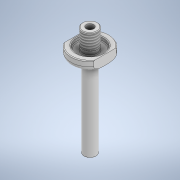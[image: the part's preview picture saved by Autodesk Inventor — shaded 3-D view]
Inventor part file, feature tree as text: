
AUTODESK INVENTOR PART (.ipt)
format: ipt  version: 2021 (Build 250183000, 183)  size: 212,992 bytes
history: native  units: mm
features: extrude x6, sketch x6, fillet x5, chamfer x2, thread x1, projected_geometry x1
ambient origin geometry x8: Origin, YZ Plane, XZ Plane, XY Plane, X Axis, Y Axis, Z Axis, Center Point
bodies: Solid1 (feature_tree)
feature tree (21):
  extrude  "Extrusion1"  Depth=3.2mm TaperAngle=0.0deg
  extrude  "Extrusion2"  Depth=0.25mm
  fillet  "Fillet1"  Radius=1.32mm
  fillet  "Fillet6"  Radius=0.25mm
  extrude  "Extrusion3"  Depth=2.0mm TaperAngle=0.0deg
  chamfer  "Chamfer2"  Distance=2.0mm Angle=45.0deg
  chamfer  "Chamfer3"  Distance=2.0mm Angle=45.0deg
  extrude  "Extrusion4"  Depth=27.5mm TaperAngle=0.0deg
  extrude  "Extrusion5"  TaperAngle=0.0deg  [1 undecoded]
  thread  "Thread1"  [1 undecoded]
  fillet  "Fillet2"  Radius=0.219mm
  fillet  "Fillet3"  Radius=0.248mm
  extrude  "Extrusion6"  Depth=10.0mm TaperAngle=0.0deg
  fillet  "Fillet5"  Radius=0.25mm
  sketch  "Sketch1"  dims[d0=12.5mm d1=3.2mm d2=0.0mm]
  sketch  "Sketch2"  dims[d3=4.63mm d4=8.9mm d5=1.32mm d6=0.0mm d7=0.25mm]
  sketch  "Sketch3"  dims[d8=5.0mm d9=5.3mm d10=0.0mm d14=0.2mm d15=2.0mm d16=45.0deg d17=0.15mm d18=2.0mm d19=45.0deg]
  sketch  "Sketch4"  dims[d20=4.0mm d21=27.5mm d22=0.0mm]
  projected_geometry  "Projected Loop1"
  sketch  "Sketch5"  dims[d23=2.5mm d24=0.0mm d25=0.0mm d26=5.6mm d27=0.0mm d28=0.219mm d29=0.248mm]
  sketch  "Sketch6"  dims[d30=10.0mm d31=10.0mm d32=0.0mm d34=0.25mm d35=1.5mm]
note: 2 required parameter values undecoded (feature->parameter linkage not recoverable at this tier; creation-order binding heuristic only, values carry confidence <= 0.55)
